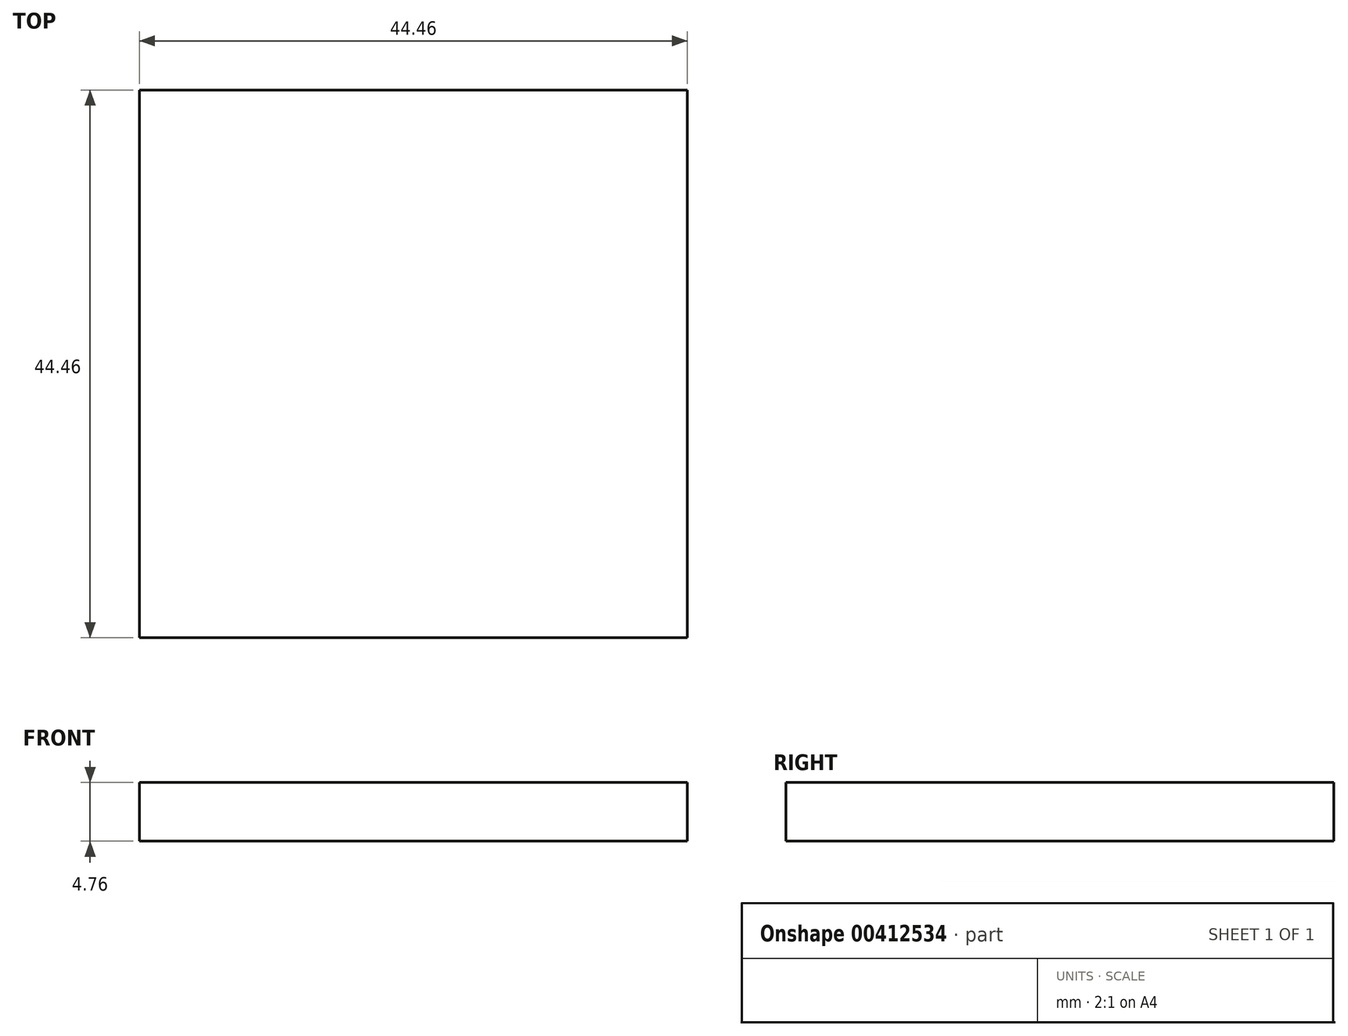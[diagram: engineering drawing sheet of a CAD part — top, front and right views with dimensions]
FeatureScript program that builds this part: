
annotation { "Feature Type Name" : "Feature", "Feature Type Description" : "" }
export const myFeature = defineFeature(function(context is Context, id is Id, definition is map)
    precondition{}
    {
        {
            var Q0;
            Q0=qCreatedBy(makeId("Top.planeOp"),FACE);
            var sketch = newSketch(context, id + "F0", { "sketchPlane" : qUnion([Q0])});
            skLineSegment(sketch, "E0.bottom", {"start": v(22.22, 22.23) * mm, "end": v(-22.23, 22.23) * mm});
            skLineSegment(sketch, "E0.top", {"start": v(22.23, -22.23) * mm, "end": v(-22.22, -22.23) * mm});
            skLineSegment(sketch, "E0.left", {"start": v(22.22, 22.23) * mm, "end": v(22.23, -22.23) * mm});
            skLineSegment(sketch, "E0.right", {"start": v(-22.23, 22.23) * mm, "end": v(-22.22, -22.23) * mm});
            skPoint(sketch, "E0.middle", {"position": v(0, 0) * mm});
            skSolve(sketch);
        }
        {
            var Q0;
            Q0 = qSketchRegion(id + "F0", true);
            extrude(context, id + "F1", {"entities" : qUnion([Q0]), "depth" : 4.76 * mm});
        }
    });
